# Revit family: QF_ACFRI_AR80-HRUC_AR80-HRUC_CU-RL.190709093255
name_source: partatom
category: Specialty Equipment
revit_build: Autodesk Revit 2016 (Build: 20150220_1215(x64)
units: mm (PartAtom-declared; Revit-internal decimal feet)

## family parameters
Always vertical = Yes
Cut with Voids When Loaded = No
OmniClass Number = 23.40.40.14
OmniClass Title = Food Service Equipment
Part Type = Normal
Room Calculation Point = No
Round Connector Dimension = Use Diameter
Shared = No
Work Plane-Based = No

## types (1)
- AR80-HRUC_400V/0Ph/50Hz
    Accessoires = No
    Consommation d'énergie minimale = 0 A
    Cost = 0 $
    Câble de connexion à l'appareil inclus = No
    Description = CELLULE SÉRIE COMPACT À CHARIOT REFROIDISSEMENT RAPIDE, GROUPE À AIR BASIC MONTÉ
    Fréquence = 50 Hz
    Hauteur hors tout = 2360 mm  [stored 7.74278 ft]
    Intensité nominale courant electrique = 15 A
    Longueur hors tout = 795 mm  [stored 2.60827 ft]
    Manufacturer = ACFRI
    Model = AR80-HRUC
    Nombres de Pôles = 1
    Phase = 1
    Poids net à vide = 0.00 kg
    Profondeur hors tout = 1145 mm  [stored 3.75656 ft]
    Protection de l'Appareil = 0 A
    Puissance Apparente = 5635 VA
    Puissance électrique  = 5635 W
    Tension = 400 V
    URL = www.acfri.com

note: [stored X ft] marks values corroborated as IEEE doubles in the binary element streams (Revit-internal decimal feet)

## geometry (parser evidence)
native form markers: Sweep x10
no freeform markers — native parametric forms only
